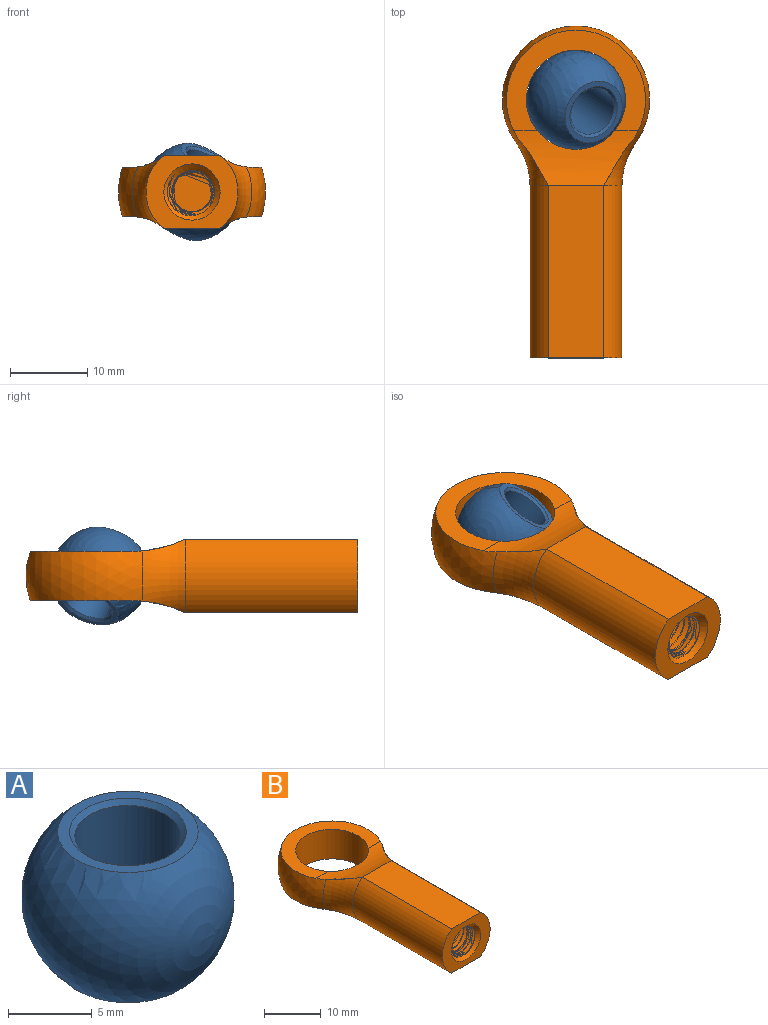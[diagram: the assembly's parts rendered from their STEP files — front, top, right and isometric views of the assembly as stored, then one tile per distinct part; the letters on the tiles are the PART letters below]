
ASSEMBLY  parts=2 mates=1
PART A: 6 faces, bbox 12.7x12.7x12.7 mm
  f0: sphere r=6.35mm, area 380mm2, adj f1,f2
  f1: plane 8.4x8.4mm, normal (0,0,1), area 17.1mm2, adj f0,f5
  f2: plane 8.4x8.4mm, normal (0,0,-1), area 17.1mm2, adj f0,f4
  f3: cylinder r=3.17mm len=8.89mm, axis (0,0,1), area 177.3mm2, adj f4,f5
  f4: cone r=3.49mm half-angle=45deg, axis (0,0,-1), area 9.4mm2, adj f2,f3
  f5: cone r=3.49mm half-angle=45deg, axis (0,0,1), area 9.4mm2, adj f1,f3
PART B: 19 faces, bbox 19.7x43.6x19.7 mm
  f0: torus R=15.47mm, axis (0,-1,0), area 52.1mm2, adj f2,f13,f16,f17
  f1: plane 11.89x9.53mm, normal (0,-1,0), area 58.2mm2, adj f2,f3,f4,f10,f11
  f2: cylinder r=5.94mm len=22.22mm, axis (0,1,0), area 245.5mm2, adj f0,f1,f10,f11
  f3: cylinder r=5.94mm len=22.22mm, axis (0,1,0), area 245.5mm2, adj f1,f10,f11,f12
  f4: cone r=3.63mm half-angle=45deg, axis (0,-1,0), area 21.4mm2, adj f1,f6,f7,f8,f9
  f5: plane 6.15x6.13mm, normal (0,-1,0), area 26.2mm2, adj f6,f7,f8,f9
  f6: bspline ~17.35x6.35mm, area 227.2mm2, adj f4,f5,f7,f9
  f7: bspline ~16.78x5.17mm, area 33.3mm2, adj f4,f5,f6,f8
  f8: bspline ~17.91x6.35mm, area 226.8mm2, adj f4,f5,f7,f9
  f9: cylinder r=3.17mm len=17.01mm, axis (0,-1,0), area 30.2mm2, adj f4,f5,f6,f8
  f10: plane 22.22x7.11mm, normal (0,0,1), area 158mm2, adj f1,f2,f3,f16
  f11: plane 22.22x7.11mm, normal (0,0,-1), area 158mm2, adj f1,f2,f3,f17
  f12: torus R=15.47mm, axis (0,-1,0), area 52.1mm2, adj f3,f13,f16,f17
  f13: sphere r=9.53mm, area 269.5mm2, adj f0,f12,f14,f15,f16,f17
  f14: plane 17.96x13mm, normal (0,0,1), area 83.8mm2, adj f13,f16,f18
  f15: plane 18.66x13.7mm, normal (0,0,-1), area 83.8mm2, adj f13,f17,f18
  f16: cylinder r=16.67mm len=16.06mm, axis (-1,0,0), area 67.8mm2, adj f0,f10,f12,f13,f14,f18
  f17: cylinder r=16.67mm len=16.06mm, axis (1,0,0), area 67.8mm2, adj f0,f11,f12,f13,f15,f18
  f18: cylinder r=6.41mm len=12.83mm, axis (0,0,1), area 255.9mm2, adj f14,f15,f16,f17
PLACE A rot(axis=(0.4,0.06,0.92),99.3deg) t=(-1.2,9.99,2.69)mm
PLACE B t=(-15.14,-8.4,9.86)mm fixed
MATE ball B.f18 <-> A.f3  axis (0,0,1) through (-15.14,7.48,9.86)mm
